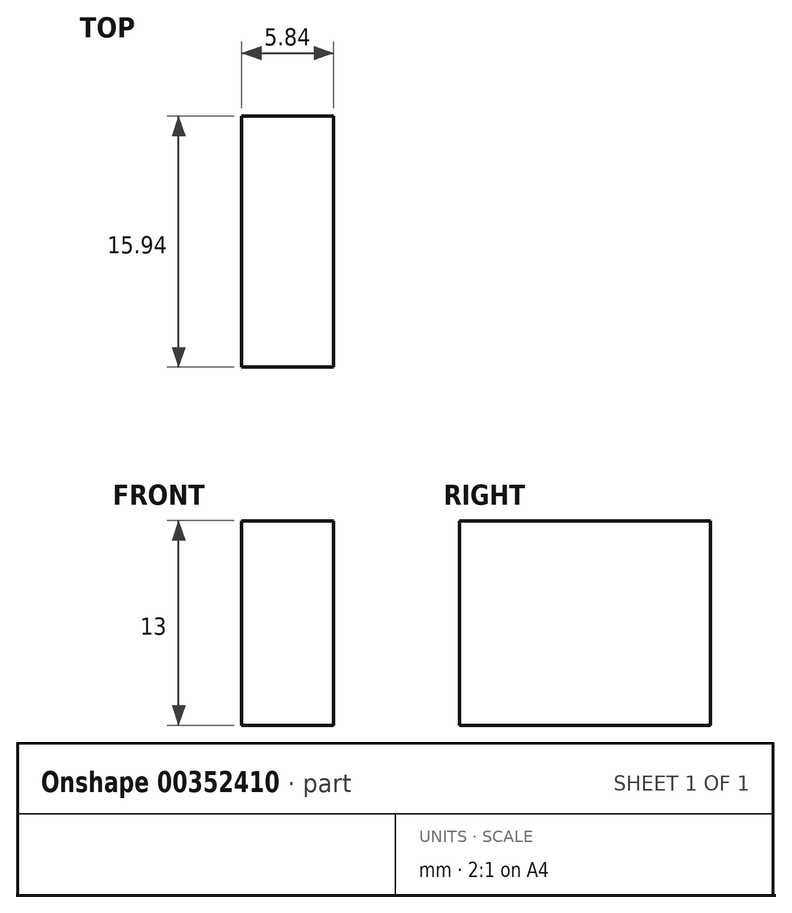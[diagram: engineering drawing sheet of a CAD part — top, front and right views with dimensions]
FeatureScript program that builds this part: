
annotation { "Feature Type Name" : "Feature", "Feature Type Description" : "" }
export const myFeature = defineFeature(function(context is Context, id is Id, definition is map)
    precondition{}
    {
        {
            var Q0;
            Q0=qCreatedBy(makeId("Right.planeOp"),FACE);
            var sketch = newSketch(context, id + "F0", { "sketchPlane" : qUnion([Q0])});
            skLineSegment(sketch, "E0.bottom", {"start": v(7.97, 6.5) * mm, "end": v(-7.97, 6.5) * mm});
            skLineSegment(sketch, "E0.top", {"start": v(7.97, -6.5) * mm, "end": v(-7.97, -6.5) * mm});
            skLineSegment(sketch, "E0.left", {"start": v(7.97, 6.5) * mm, "end": v(7.97, -6.5) * mm});
            skLineSegment(sketch, "E0.right", {"start": v(-7.97, 6.5) * mm, "end": v(-7.97, -6.5) * mm});
            skPoint(sketch, "E0.middle", {"position": v(0, 0) * mm});
            skSolve(sketch);
        }
        {
            var Q0;
            Q0=makeQuery(id+"F0.imprint","IMPRINT",FACE,{"disambiguationData":[TD([[makeQuery(id+"F0.imprint","IMPRINT",EDGE,{"derivedFrom":sQuery(id+"F0.wireOp",EDGE,"E0.bottom")}),1.0]])]});
            extrude(context, id + "F1", {"entities" : qUnion([Q0]), "depth" : 5.84 * mm});
        }
    });
